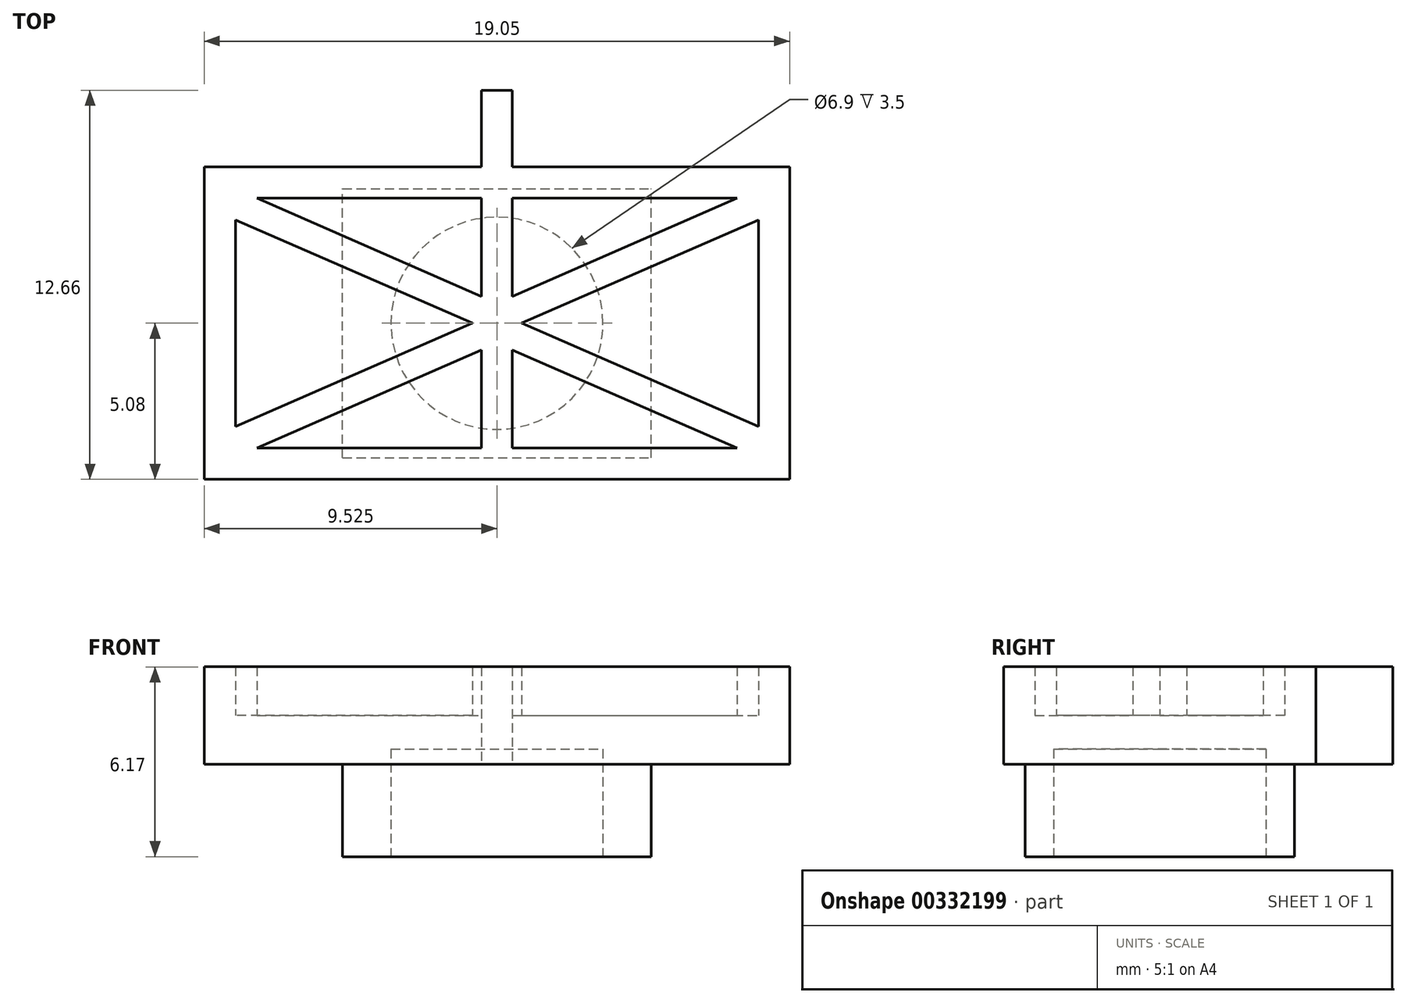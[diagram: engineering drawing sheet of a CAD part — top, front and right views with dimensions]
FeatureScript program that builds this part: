
annotation { "Feature Type Name" : "Feature", "Feature Type Description" : "" }
export const myFeature = defineFeature(function(context is Context, id is Id, definition is map)
    precondition{}
    {
        {
            var Q0;
            Q0=qCreatedBy(makeId("Top.planeOp"),FACE);
            var sketch = newSketch(context, id + "F0", { "sketchPlane" : qUnion([Q0])});
            skLineSegment(sketch, "E0.bottom", {"start": v(-19.05, 10.16) * mm, "end": v(0, 10.16) * mm});
            skLineSegment(sketch, "E0.top", {"start": v(-19.05, 0) * mm, "end": v(0, 0) * mm});
            skLineSegment(sketch, "E0.left", {"start": v(-19.05, 10.16) * mm, "end": v(-19.05, 0) * mm});
            skLineSegment(sketch, "E0.right", {"start": v(0, 10.16) * mm, "end": v(0, 0) * mm});
            skLineSegment(sketch, "E1", {"start": v(-9.52, 10.16) * mm, "end": v(-9.52, 0) * mm, "construction": true});
            skLineSegment(sketch, "E2.bottom", {"start": v(-10.02, 12.66) * mm, "end": v(-9.02, 12.66) * mm});
            skLineSegment(sketch, "E2.top", {"start": v(-10.02, 10.16) * mm, "end": v(-9.02, 10.16) * mm});
            skLineSegment(sketch, "E2.left", {"start": v(-10.02, 12.66) * mm, "end": v(-10.02, 10.16) * mm});
            skLineSegment(sketch, "E2.right", {"start": v(-9.02, 12.66) * mm, "end": v(-9.02, 10.16) * mm});
            skSolve(sketch);
        }
        {
            var Q0;
            Q0=qSketchRegion(id+"F0",true);
            extrude(context, id + "F1", {"entities" : qUnion([Q0]), "depth" : 3.17 * mm});
        }
        {
            var Q0;
            Q0=makeQuery(id+"F1.opExtrude","CAP_FACE",FACE,{"disambiguationData":[OSD([sQuery(id+"F0.wireOp",EDGE,"E0.bottom"),sQuery(id+"F0.wireOp",EDGE,"E0.top"),sQuery(id+"F0.wireOp",EDGE,"E0.left"),sQuery(id+"F0.wireOp",EDGE,"E0.right")])],"isStart":false});
            var sketch = newSketch(context, id + "F2", { "sketchPlane" : qUnion([Q0])});
            skLineSegment(sketch, "E3.bottom", {"start": v(-18.03, 9.14) * mm, "end": v(-1.02, 9.14) * mm});
            skLineSegment(sketch, "E3.top", {"start": v(-18.03, 1.02) * mm, "end": v(-1.02, 1.02) * mm});
            skLineSegment(sketch, "E3.left", {"start": v(-18.03, 9.14) * mm, "end": v(-18.03, 1.02) * mm});
            skLineSegment(sketch, "E3.right", {"start": v(-1.02, 9.14) * mm, "end": v(-1.02, 1.02) * mm});
            skSolve(sketch);
        }
        {
            var Q0;
            Q0=qSketchRegion(id+"F2",true);
            extrude(context, id + "F3", {"entities" : qUnion([Q0]), "operationType" : NewBodyOperationType.REMOVE, "oppositeDirection" : true, "depth" : 1.59 * mm});
        }
        {
            var Q0;
            {var subQ1=sQuery(id+"F2.wireOp",EDGE,"E3.top");var subQ4=makeQuery(id+"F3.boolean.opBoolean","COPY",FACE,{"derivedFrom":makeQuery(id+"F3.opExtrude","SWEPT_FACE",FACE,{"disambiguationData":[OSD([subQ1])]})});var subQ6=sQuery(id+"F2.wireOp",EDGE,"E3.right");Q0=makeQuery(id+"FbiU5rRMadnEj1Y_1.boolean.opBoolean","SPLIT",FACE,{"disambiguationData":[TD([subQ4])],"derivedFrom":makeQuery(id+"FD6hazfNaiJcgqe_1.boolean.opBoolean","SPLIT",FACE,{"disambiguationData":[TD([subQ4])],"derivedFrom":makeQuery(id+"F3.boolean.opBoolean","COPY",FACE,{"derivedFrom":makeQuery(id+"F3.opExtrude","CAP_FACE",FACE,{"disambiguationData":[OSD([sQuery(id+"F2.wireOp",EDGE,"E3.bottom"),subQ1,sQuery(id+"F2.wireOp",EDGE,"E3.left"),subQ6])],"isStart":false})})})});}
            var sketch = newSketch(context, id + "F4", { "sketchPlane" : qUnion([Q0])});
            skLineSegment(sketch, "E4", {"start": v(-19.05, 1.68) * mm, "end": v(-1.02, 1.68) * mm, "construction": true});
            skLineSegment(sketch, "E5", {"start": v(-9.53, 10.16) * mm, "end": v(-9.53, 0) * mm, "construction": true});
            skSolve(sketch);
        }
        {
            var Q0;
            Q0=makeQuery(id+"F1.opExtrude","CAP_FACE",FACE,{"disambiguationData":[OSD([sQuery(id+"F0.wireOp",EDGE,"E0.bottom"),sQuery(id+"F0.wireOp",EDGE,"E0.top"),sQuery(id+"F0.wireOp",EDGE,"E0.left"),sQuery(id+"F0.wireOp",EDGE,"E0.right"),sQuery(id+"F0.wireOp",EDGE,"iD4YVwzi-38ZZ-sZow-cuPB-LK5aPxXRs2tg"),sQuery(id+"F0.wireOp",EDGE,"25aa8db4-dd9b-41d2-b8c9-1594e9b75191"),sQuery(id+"F0.wireOp",EDGE,"40f63cb3-13d8-4821-a3c4-c05e674bd89b0.MirrorC")])],"isStart":true});
            var sketch = newSketch(context, id + "F5", { "sketchPlane" : qUnion([Q0])});
            skLineSegment(sketch, "E6.bottom", {"start": v(-14.55, -0.7) * mm, "end": v(-4.5, -0.7) * mm});
            skLineSegment(sketch, "E6.top", {"start": v(-14.55, -9.46) * mm, "end": v(-4.5, -9.46) * mm});
            skLineSegment(sketch, "E6.left", {"start": v(-14.55, -0.7) * mm, "end": v(-14.55, -9.46) * mm});
            skLineSegment(sketch, "E6.right", {"start": v(-4.5, -0.7) * mm, "end": v(-4.5, -9.46) * mm});
            skSolve(sketch);
        }
        {
            var Q0;
            Q0=qSketchRegion(id+"F5",true);
            extrude(context, id + "F6", {"entities" : qUnion([Q0]), "operationType" : NewBodyOperationType.ADD, "depth" : 3 * mm, "offsetDistance" : 25 * mm});
        }
        {
            var Q0;
            Q0=makeQuery(id+"F6.opExtrude","CAP_FACE",FACE,{"disambiguationData":[OSD([sQuery(id+"F5.wireOp",EDGE,"E6.bottom"),sQuery(id+"F5.wireOp",EDGE,"E6.top"),sQuery(id+"F5.wireOp",EDGE,"E6.left"),sQuery(id+"F5.wireOp",EDGE,"E6.right")])],"isStart":false});
            var sketch = newSketch(context, id + "F7", { "sketchPlane" : qUnion([Q0])});
            skCircle(sketch, "E7", {"center": v(-9.52, -5.08) * mm, "radius": 3.45 * mm});
            skLineSegment(sketch, "E8", {"start": v(-19.05, -5.08) * mm, "end": v(0, -5.08) * mm, "construction": true});
            skPoint(sketch, "E8.endSnap0", {"position": v(-4.5, -5.08) * mm});
            skLineSegment(sketch, "E9", {"start": v(-9.53, 0) * mm, "end": v(-9.53, -9.46) * mm, "construction": true});
            skSolve(sketch);
        }
        {
            var Q0;
            Q0=makeQuery(id+"F7.imprint","IMPRINT",FACE,{"disambiguationData":[TD([[makeQuery(id+"F7.imprint","IMPRINT",EDGE,{"derivedFrom":sQuery(id+"F7.wireOp",EDGE,"E7")}),1.0]])]});
            extrude(context, id + "F8", {"entities" : qUnion([Q0]), "operationType" : NewBodyOperationType.REMOVE, "oppositeDirection" : true, "depth" : 3.5 * mm, "offsetDistance" : 25 * mm});
        }
        {
            var Q0;
            Q0=makeQuery(id+"F4.imprint","IMPRINT",FACE,{"disambiguationData":[TD([[makeQuery(id+"F4.imprint","IMPRINT",EDGE,{"derivedFrom":makeQuery(id+"F3.boolean.opBoolean","COPY",EDGE,{"derivedFrom":makeQuery(id+"F3.opExtrude","CAP_EDGE",EDGE,{"disambiguationData":[OSD([sQuery(id+"F2.wireOp",EDGE,"E3.bottom")])],"isStart":false})})}),-1.0]])]});
            var sketch = newSketch(context, id + "F9", { "sketchPlane" : qUnion([Q0])});
            skLineSegment(sketch, "E10", {"start": v(-1.72, 9.14) * mm, "end": v(-9.53, 5.74) * mm});
            skLineSegment(sketch, "E11", {"start": v(-8.73, 5.08) * mm, "end": v(-1.02, 8.44) * mm});
            skLineSegment(sketch, "E12", {"start": v(-1.02, 8.44) * mm, "end": v(-1.02, 9.14) * mm});
            skLineSegment(sketch, "E13", {"start": v(-1.02, 9.14) * mm, "end": v(-1.72, 9.14) * mm});
            skLineSegment(sketch, "E14", {"start": v(-19.05, 5.08) * mm, "end": v(0, 5.08) * mm, "construction": true});
            skLineSegment(sketch, "E15.MirrorCS", {"start": v(-17.33, 9.14) * mm, "end": v(-9.53, 5.74) * mm});
            skLineSegment(sketch, "E16.MirrorCS", {"start": v(-10.33, 5.08) * mm, "end": v(-18.03, 8.44) * mm});
            skLineSegment(sketch, "E17.MirrorCS", {"start": v(-18.03, 8.44) * mm, "end": v(-18.03, 9.14) * mm});
            skLineSegment(sketch, "E18.MirrorCS", {"start": v(-18.03, 9.14) * mm, "end": v(-17.33, 9.14) * mm});
            skLineSegment(sketch, "E19.MirrorCS", {"start": v(-10.33, 5.08) * mm, "end": v(-18.03, 1.72) * mm});
            skLineSegment(sketch, "E20.MirrorCS", {"start": v(-8.73, 5.08) * mm, "end": v(-1.02, 1.72) * mm});
            skLineSegment(sketch, "E21.MirrorCS", {"start": v(-1.72, 1.02) * mm, "end": v(-9.53, 4.42) * mm});
            skLineSegment(sketch, "E22.MirrorCS", {"start": v(-17.33, 1.02) * mm, "end": v(-9.53, 4.42) * mm});
            skLineSegment(sketch, "E23.MirrorCS", {"start": v(-18.03, 1.02) * mm, "end": v(-17.33, 1.02) * mm});
            skLineSegment(sketch, "E24.MirrorCS", {"start": v(-18.03, 1.72) * mm, "end": v(-18.03, 1.02) * mm});
            skLineSegment(sketch, "E25.MirrorCS", {"start": v(-1.02, 1.72) * mm, "end": v(-1.02, 1.02) * mm});
            skLineSegment(sketch, "E26.MirrorCS", {"start": v(-1.02, 1.02) * mm, "end": v(-1.72, 1.02) * mm});
            skLineSegment(sketch, "E27.bottom", {"start": v(-10.03, 9.14) * mm, "end": v(-9.03, 9.14) * mm});
            skLineSegment(sketch, "E27.top", {"start": v(-10.03, 1.02) * mm, "end": v(-9.03, 1.02) * mm});
            skLineSegment(sketch, "E27.left", {"start": v(-10.03, 9.14) * mm, "end": v(-10.03, 1.02) * mm});
            skLineSegment(sketch, "E27.right", {"start": v(-9.03, 9.14) * mm, "end": v(-9.03, 1.02) * mm});
            skSolve(sketch);
        }
        {
            var Q0;
            Q0=qSketchRegion(id+"F9",true);
            var Q1;
            Q1=makeQuery(id+"FXsS83p9KQ4uv0L_1.boolean.opBoolean","MERGE",FACE,{"derivedFrom":[makeQuery(id+"F1.opExtrude","CAP_FACE",FACE,{"disambiguationData":[OSD([sQuery(id+"F0.wireOp",EDGE,"E0.bottom"),sQuery(id+"F0.wireOp",EDGE,"E0.top"),sQuery(id+"F0.wireOp",EDGE,"E0.left"),sQuery(id+"F0.wireOp",EDGE,"E0.right"),sQuery(id+"F0.wireOp",EDGE,"25aa8db4-dd9b-41d2-b8c9-1594e9b75191"),sQuery(id+"F0.wireOp",EDGE,"40f63cb3-13d8-4821-a3c4-c05e674bd89b0.MirrorC")])],"isStart":false}),makeQuery(id+"FbiU5rRMadnEj1Y_1.opExtrude","CAP_FACE",FACE,{"disambiguationData":[OSD([sQuery(id+"FmV1InaubWQgJeV_1.wireOp",EDGE,"lTleeF4S-0pnc-dI25-KJAR-2TLCTf0jWGc3"),sQuery(id+"FmV1InaubWQgJeV_1.wireOp",EDGE,"m9JDErra-axgF-Q1Zk-CJc0-x6RwavRCbCz8")])],"isStart":false}),makeQuery(id+"FXsS83p9KQ4uv0L_1.opExtrude","CAP_FACE",FACE,{"disambiguationData":[OSD([sQuery(id+"Fi3yzKCDt9pSW51_1.wireOp",EDGE,"cutzoVbR-JFbv-1kZ0-SQrw-pSLFGMZcN76v"),sQuery(id+"Fi3yzKCDt9pSW51_1.wireOp",EDGE,"XYQyWRLz-35l4-wHee-0FsY-Oat0KQk3jhR6"),sQuery(id+"Fi3yzKCDt9pSW51_1.wireOp",EDGE,"lBgadLLx-aQS8-kMAZ-d5qN-Zo8duSUxtBeX"),sQuery(id+"Fi3yzKCDt9pSW51_1.wireOp",EDGE,"DlRPRQGx-Alaq-SPUL-URFH-jddu6C2Nnp9z"),sQuery(id+"Fi3yzKCDt9pSW51_1.wireOp",EDGE,"Shc4e2eY-gIsf-lYKj-D0sO-212MCfLGw1w2"),sQuery(id+"Fi3yzKCDt9pSW51_1.wireOp",EDGE,"DXv1RSob-CDWK-uPmN-nh2c-bdjhB3yjVnB2"),sQuery(id+"Fi3yzKCDt9pSW51_1.wireOp",EDGE,"Mjf90MPI-7UZW-OfA1-fD3l-TGEU1IJ1uaYu"),sQuery(id+"Fi3yzKCDt9pSW51_1.wireOp",EDGE,"IrneLFi4-a4Xm-RgwH-oJvY-WcCPALNDAReP"),sQuery(id+"Fi3yzKCDt9pSW51_1.wireOp",EDGE,"toQdHavX-h7D1-dxbV-IXrh-P84p4AImceJh"),sQuery(id+"Fi3yzKCDt9pSW51_1.wireOp",EDGE,"xGw8HYbu-oKFY-4S3u-lNNy-w4TfAhwJFqQu"),sQuery(id+"Fi3yzKCDt9pSW51_1.wireOp",EDGE,"5pvZd2gl-M8UA-9HNZ-daD7-4TEjzgTyMgsA"),sQuery(id+"Fi3yzKCDt9pSW51_1.wireOp",EDGE,"b1702624-0c59-4015-bc2e-a5f6b81265a70.MirrorCS"),sQuery(id+"Fi3yzKCDt9pSW51_1.wireOp",EDGE,"7deeccc9-7886-4666-b44c-47b900ed28990.MirrorCS"),sQuery(id+"Fi3yzKCDt9pSW51_1.wireOp",EDGE,"75936777-967d-44d6-aacf-753113c8b50b0.MirrorCS"),sQuery(id+"Fi3yzKCDt9pSW51_1.wireOp",EDGE,"e5875930-5b2f-47d0-b261-f87a419dd3ea0.MirrorCS"),sQuery(id+"Fi3yzKCDt9pSW51_1.wireOp",EDGE,"e1f8200d-9078-41b5-85b4-8a4adb8dc9e80.MirrorCS"),sQuery(id+"Fi3yzKCDt9pSW51_1.wireOp",EDGE,"40fd4d9e-f758-4b42-b7b5-3e08d0cf58f50.MirrorCS"),sQuery(id+"Fi3yzKCDt9pSW51_1.wireOp",EDGE,"553d3a6c-e9a7-4b40-b1d3-0817f640e5cc0.MirrorCS"),sQuery(id+"Fi3yzKCDt9pSW51_1.wireOp",EDGE,"5a723a2c-c48e-43ea-a32e-a11b15ff1a7b0.MirrorCS"),sQuery(id+"Fi3yzKCDt9pSW51_1.wireOp",EDGE,"932d58c0-4b54-410d-a467-0e9cf49887c90.MirrorCS"),sQuery(id+"Fi3yzKCDt9pSW51_1.wireOp",EDGE,"eeedfdb4-aa26-4e83-bf33-b18388155c4d0.MirrorCS"),sQuery(id+"Fi3yzKCDt9pSW51_1.wireOp",EDGE,"a4c71cba-da55-4cc9-80cf-8947727491d80.MirrorCS")])],"isStart":false})]});
            extrude(context, id + "F10", {"entities" : qUnion([Q0]), "operationType" : NewBodyOperationType.ADD, "endBound" : BoundingType.UP_TO_SURFACE, "depth" : 25 * mm, "endBoundEntityFace" : qUnion([Q1]), "offsetDistance" : 25 * mm});
        }
    });
